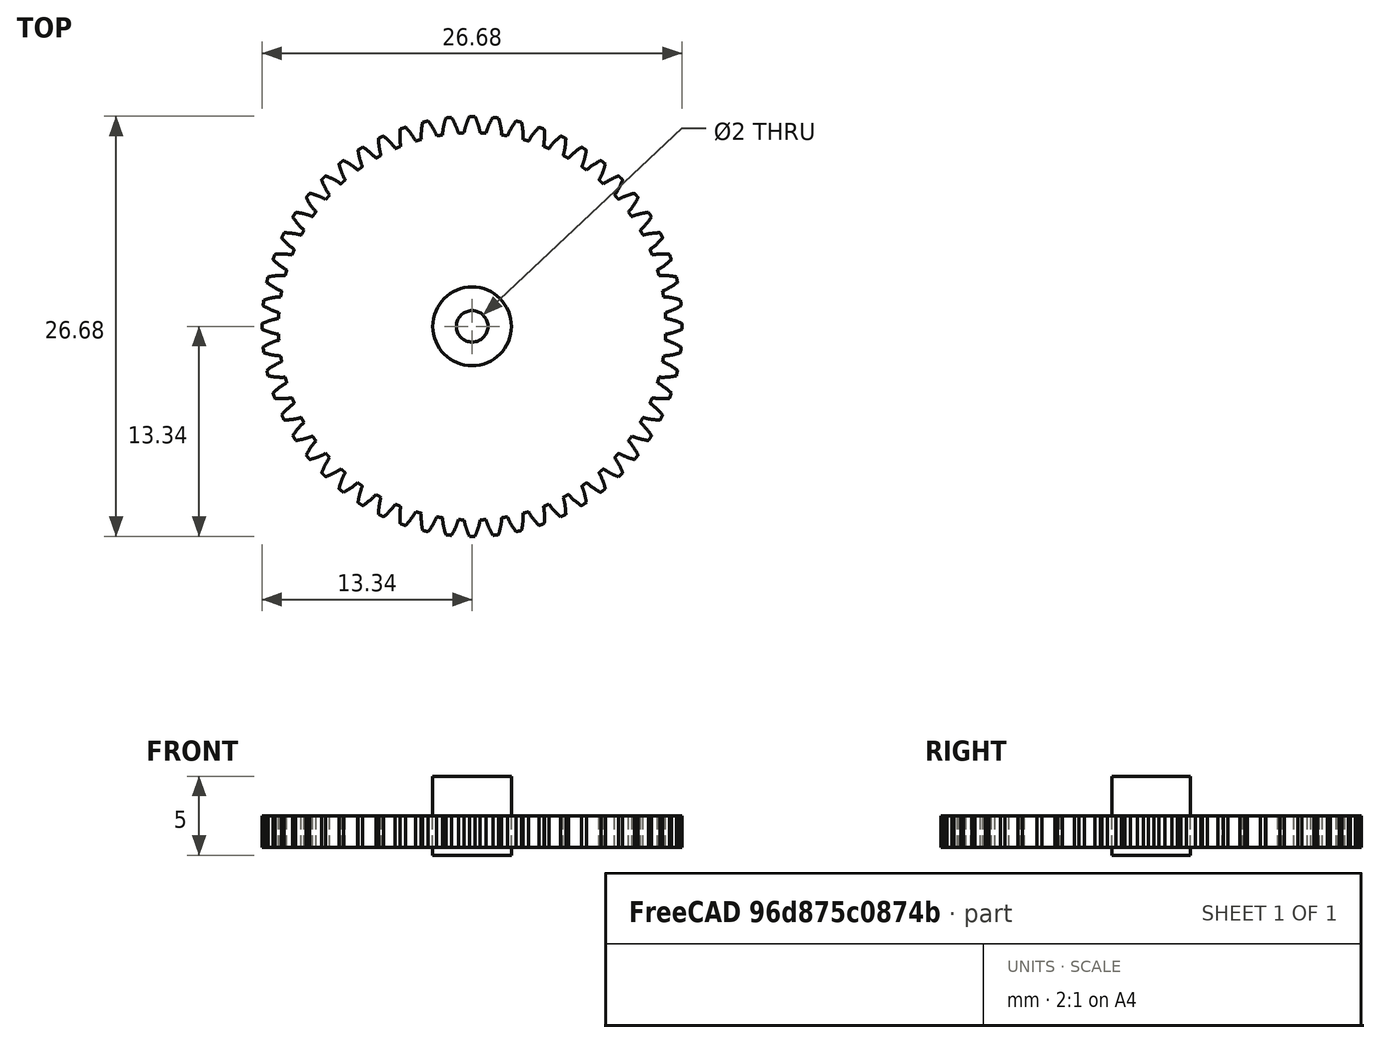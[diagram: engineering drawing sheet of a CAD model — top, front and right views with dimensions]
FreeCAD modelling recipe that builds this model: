
FCSTD DOCUMENT  (FreeCAD 0.17R11129 (Git))
Label: Servo_Gear
License: All rights reserved
LicenseURL: http://en.wikipedia.org/wiki/All_rights_reserved
objects: Part::Cylinder×2, Part::FeaturePython×1, Image::ImagePlane×1, Part::MultiFuse×1, Part::Cut×1, Part::Part2DObjectPython×1
note: 6 computed .brp shape members not serialized (recipe doc carries the construction recipe); baked Part::Feature solids carry a one-line shape summary decoded from their .brp

FEATURE [Part::FeaturePython] InvoluteGear  # WARN: FeaturePython — macro-defined, semantics opaque (R4)
  backlash = 0
  beta = 0
  clearance = 0.25
  head = 0
  height = 2
  module = 0.46
  numpoints = 6
  pressure_angle = 20
  reversed_backlash = false
  shift = 0
  simple = false
  teeth = 56
  undercut = false
FEATURE [Image::ImagePlane] ImagePlane
  Placement = pos=(0,0,-22) rot=(0,0,1;0rad)
  XSize = 27
  YSize = 27
FEATURE [Part::Cylinder] Cylinder
  Angle = 360
  AttacherType = Attacher::AttachEngine3D
  Height = 5
  Placement = pos=(0,0,-0.5) rot=(0,0,1;0rad)
  Radius = 2.5
FEATURE [Part::Cylinder] Cylinder001
  Angle = 360
  AttacherType = Attacher::AttachEngine3D
  Height = 5
  Placement = pos=(0,0,-0.5) rot=(0,0,1;0rad)
  Radius = 1
FEATURE [Part::MultiFuse] Fusion
  Shapes = -> [InvoluteGear,Cylinder]
FEATURE [Part::Cut] Cut
  Base = -> Fusion
  Tool = -> Cylinder001
FEATURE [Part::Part2DObjectPython] Shape2DView  # Draft 2D object (typed FeaturePython)
  Base = -> Cut
  FaceNumbers = [4]
  HiddenLines = false
  InPlace = true
  Placement = pos=(0,0,-21.9) rot=(0,0,1;0rad)
  Projection = (0,0,1)
  ProjectionMode = 0
  SegmentLength = 0.05
  Tessellation = false
